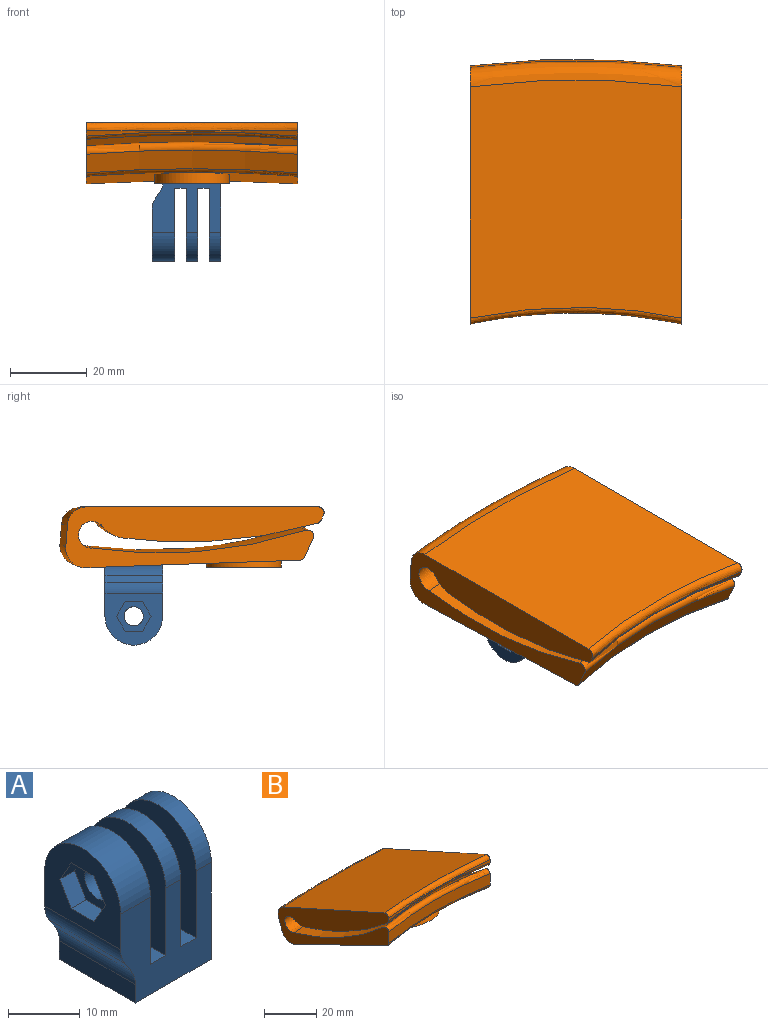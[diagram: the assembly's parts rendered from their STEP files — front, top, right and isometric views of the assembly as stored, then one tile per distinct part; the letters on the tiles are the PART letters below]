
ASSEMBLY  parts=2 mates=1
PART A: 28 faces, bbox 17.9x15x24.1 mm
  f0: plane 17.9x16.63mm, normal (0,1,0), area 208.9mm2, adj f1,f2,f5,f6,f7,f8,f11,f12
  f1: plane 15x3.15mm, normal (-1,0,0), area 47.2mm2, adj f0,f3,f26,f27
  f2: plane 24.13x15mm, normal (1,0,0), area 318.2mm2, adj f0,f3,f10,f14,f27
  f3: plane 17.9x16.63mm, normal (0,-1,0), area 208.9mm2, adj f1,f2,f5,f6,f7,f8,f11,f12
  f4: plane 9.02x7.79mm, normal (-1,0,0), area 33mm2, adj f9,f17,f18,f19,f20,f21,f22
  f5: plane 19x15mm, normal (1,0,0), area 241.2mm2, adj f0,f3,f9,f11,f16
  f6: plane 19x15mm, normal (-1,0,0), area 241.2mm2, adj f0,f3,f11,f13,f15
  f7: plane 19x15mm, normal (1,0,0), area 241.2mm2, adj f0,f3,f12,f13,f15
  f8: plane 19x15mm, normal (-1,0,0), area 241.2mm2, adj f0,f3,f10,f12,f14
  f9: cylinder r=2.5mm len=5mm, axis (-1,0,0), area 47.1mm2, adj f4,f5
  f10: cylinder r=2.5mm len=5mm, axis (-1,0,0), area 47.1mm2, adj f2,f8
  f11: plane 15x3mm, normal (0,0,1), area 45mm2, adj f0,f3,f5,f6
  f12: plane 15x3mm, normal (0,0,1), area 45mm2, adj f0,f3,f7,f8
  f13: cylinder r=2.5mm len=5mm, axis (-1,0,0), area 47.1mm2, adj f6,f7
  f14: cylinder r=7.5mm len=15mm, axis (1,0,0), area 70.7mm2, adj f0,f2,f3,f8
  f15: cylinder r=7.5mm len=15mm, axis (1,0,0), area 70.7mm2, adj f0,f3,f6,f7
  f16: cylinder r=7.5mm len=15mm, axis (1,0,0), area 139mm2, adj f0,f3,f5,f23
  f17: plane 3.9x2.9mm, normal (0,-0.87,0.5), area 13.1mm2, adj f4,f18,f22,f23
  f18: plane 3.9x2.9mm, normal (0,-0.87,-0.5), area 13.1mm2, adj f4,f17,f19,f23
  f19: plane 4.5x2.9mm, normal (0,0,-1), area 13.1mm2, adj f4,f18,f20,f23
  f20: plane 3.9x2.9mm, normal (0,0.87,-0.5), area 13.1mm2, adj f4,f19,f21,f23
  f21: plane 3.9x2.9mm, normal (0,0.87,0.5), area 13.1mm2, adj f4,f20,f22,f23
  f22: plane 4.5x2.9mm, normal (0,0,1), area 13.1mm2, adj f4,f17,f21,f23
  f23: plane 15x13.57mm, normal (-1,0,0), area 126.7mm2, adj f0,f3,f16,f17,f18,f19,f20,f21
  f24: plane 15x1.95mm, normal (-0.84,0,-0.55), area 35mm2, adj f0,f3,f25,f26
  f25: cylinder r=5mm len=15mm, axis (0,-1,0), area 43.4mm2, adj f0,f3,f23,f24
  f26: cylinder r=5mm len=15mm, axis (0,-1,0), area 43.4mm2, adj f0,f1,f3,f24
  f27: plane 15x15mm, normal (0,0,-1), area 225mm2, adj f0,f1,f2,f3
PART B: 27 faces, bbox 87.7x97.5x42.4 mm
  f0: torus R=229.72mm, axis (0,0,-1), area 2993.2mm2, adj f4,f7,f8,f15,f19,f20,f21,f23
  f1: cone r=201.24mm half-angle=63.5deg, axis (0,0,-1), area 2790.1mm2, adj f7,f8,f12,f16,f17
  f2: cylinder r=146.04mm len=55mm, axis (0,0,-1), area 37.8mm2, adj f7,f8,f13,f14
  f3: torus R=225.16mm, axis (0,0,-1), area 2819.6mm2, adj f7,f8,f9,f14
  f4: torus R=198.24mm, axis (0,0,-1), area 795.9mm2, adj f0,f7,f8,f9
  f5: cylinder r=146.04mm len=55mm, axis (0,0,-1), area 294.1mm2, adj f7,f8,f15,f16
  f6: cone r=207.06mm half-angle=19.5deg, axis (0,0,1), area 320.9mm2, adj f7,f8,f11,f12
  f7: plane 61.28x41.05mm, normal (1,0,0), area 774.2mm2, adj f0,f1,f2,f3,f4,f5,f6,f9
  f8: plane 61.28x41.05mm, normal (-1,0,0), area 774.2mm2, adj f0,f1,f2,f3,f4,f5,f6,f9
  f9: torus R=192.94mm, axis (0,0,1), area 340.4mm2, adj f3,f4,f7,f8
  f10: plane 56.6x55mm, normal (0,0.41,0.91), area 3274.8mm2, adj f7,f8,f11,f13
  f11: bspline ~73.19x7.45mm, area 412.5mm2, adj f6,f7,f8,f10
  f12: torus R=198.42mm, axis (0,0,1), area 467.8mm2, adj f1,f6,f7,f8
  f13: bspline ~55.62x4.73mm, area 165.3mm2, adj f2,f7,f8,f10
  f14: torus R=147.54mm, axis (0,0,1), area 71.1mm2, adj f2,f3,f7,f8
  f15: torus R=147.54mm, axis (0,0,1), area 191.7mm2, adj f0,f5,f7,f8
  f16: torus R=147.54mm, axis (0,0,1), area 91.9mm2, adj f1,f5,f7,f8
  f17: cylinder r=9.73mm len=19.47mm, axis (0,-0.41,-0.91), area 159.2mm2, adj f1,f18
  f18: plane 19.47x17.76mm, normal (0,-0.41,-0.91), area 259.2mm2, adj f17,f26
  f19: plane 7.23x6.58mm, normal (-0.87,0.46,-0.2), area 29.6mm2, adj f0,f20,f22,f24
  f20: plane 6.21x6.09mm, normal (-0.87,-0.46,0.2), area 23.1mm2, adj f0,f19,f21,f22
  f21: plane 6.12x3.15mm, normal (0,-0.91,0.41), area 20.5mm2, adj f0,f20,f22,f23
  f22: plane 12.12x9.58mm, normal (0,0.41,0.91), area 57mm2, adj f19,f20,f21,f23,f24,f25,f26
  f23: plane 6.21x6.09mm, normal (0.87,-0.46,0.2), area 23.1mm2, adj f0,f21,f22,f25
  f24: plane 6.12x5.11mm, normal (0,0.91,-0.41), area 33.6mm2, adj f0,f19,f22,f25
  f25: plane 7.23x6.58mm, normal (0.87,0.46,-0.2), area 29.6mm2, adj f0,f22,f23,f24
  f26: cylinder r=3.5mm len=7.45mm, axis (0,0.41,0.91), area 57.2mm2, adj f18,f22
PLACE A rot(axis=(1,0,0),180deg) t=(0,0.91,-38.15)mm
PLACE B rot(axis=(1,0,0),24.2deg) t=(0,-16.76,3.02)mm
MATE parallel A.f27 <-> B.f10  axis (0,0,1) through (0,8.41,-49.52)mm
